FCSTD DOCUMENT  (FreeCAD 1.0R39109 (Git))
Label: udemyProjectModule1metricFREECAD
License: All rights reserved
objects: Part::FeaturePython×3, Sketcher::SketchObject×1
note: 5 computed .brp shape members not serialized (recipe doc carries the construction recipe); baked Part::Feature solids carry a one-line shape summary decoded from their .brp

FEATURE [Part::FeaturePython] IfcObject003  label="Building"  # WARN: FeaturePython — macro-defined, semantics opaque (R4)
  CompositionType = -1
  ElevationOfRefHeight = 0
  ElevationOfTerrain = 0
  GlobalId = 3ZR71QWXn8eBFc1LVgS9kI
  IfcClass = IfcBuilding
  ShapeMode = 0
  StepId = 23
  expr: Label2 = Description
FEATURE [Part::FeaturePython] IfcObject002  label="Site"  # WARN: FeaturePython — macro-defined, semantics opaque (R4)
  CompositionType = -1
  GlobalId = 3sOkh7jo544A_tfJeOJWge
  Group = -> [IfcObject003]
  IfcClass = IfcSite
  RefElevation = 0
  ShapeMode = 0
  StepId = 21
  expr: Label2 = Description
FEATURE [Part::FeaturePython] IfcObject001  label="_IfcProject001"  # WARN: FeaturePython — macro-defined, semantics opaque (R4)
  GlobalId = 2x7dZLKtn7CQsyYiZBJNY$
  Group = -> [IfcObject002]
  IfcClass = IfcProject
  IfcFilePath = <userpath>/github/websiteRepository/udemyCADcert/udemyProjectModule1metricFREECAD.ifc
  Modified = true
  Schema = 1
  ShapeMode = 0
  StepId = 1
  expr: Label2 = Description
FEATURE [Sketcher::SketchObject] Sketch  label="floorplan"
  ArcFitTolerance = 1e-06
  FullyConstrained = false
  MakeInternals = false
  sketch-geometry (38):
    g0: LineSegment StartX=0 StartY=0 StartZ=0 EndX=20000 EndY=0 EndZ=0
    g1: LineSegment StartX=20000 StartY=0 StartZ=0 EndX=20000 EndY=10000 EndZ=0
    g2: LineSegment StartX=20000 StartY=10000 StartZ=0 EndX=0 EndY=10000 EndZ=0
    g3: LineSegment StartX=0 StartY=10000 StartZ=0 EndX=0 EndY=0 EndZ=0
    g4: LineSegment [constr] StartX=0 StartY=5000 StartZ=0 EndX=300 EndY=5000 EndZ=0
    g5: LineSegment [constr] StartX=10000 StartY=10000 StartZ=0 EndX=10000 EndY=9700 EndZ=0
    g6: LineSegment [constr] StartX=10000 StartY=0 StartZ=0 EndX=10000 EndY=300 EndZ=0
    g7: LineSegment [constr] StartX=20000 StartY=5000 StartZ=0 EndX=19700 EndY=5000 EndZ=0
    g8: LineSegment StartX=300 StartY=300 StartZ=0 EndX=19700 EndY=300 EndZ=0
    g9: LineSegment StartX=19700 StartY=300 StartZ=0 EndX=19700 EndY=9700 EndZ=0
    g10: LineSegment StartX=19700 StartY=9700 StartZ=0 EndX=300 EndY=9700 EndZ=0
    g11: LineSegment StartX=300 StartY=9700 StartZ=0 EndX=300 EndY=300 EndZ=0
    g12: LineSegment [constr] StartX=300 StartY=9700 StartZ=0 EndX=4500 EndY=9700 EndZ=0
    g13: LineSegment StartX=4500 StartY=9700 StartZ=0 EndX=4500 EndY=6100 EndZ=0
    g14: LineSegment [constr] StartX=4500 StartY=9700 StartZ=0 EndX=4400 EndY=9700 EndZ=0
    g15: LineSegment StartX=4400 StartY=9700 StartZ=0 EndX=4400 EndY=6100 EndZ=0
    g16: LineSegment StartX=10600 StartY=9700 StartZ=0 EndX=10600 EndY=6100 EndZ=0
    g17: LineSegment StartX=10500 StartY=9700 StartZ=0 EndX=10500 EndY=6100 EndZ=0
    g18: LineSegment StartX=16600 StartY=9700 StartZ=0 EndX=16600 EndY=6100 EndZ=0
    g19: LineSegment StartX=16700 StartY=9700 StartZ=0 EndX=16700 EndY=6100 EndZ=0
    g20: LineSegment StartX=16700 StartY=9700 StartZ=0 EndX=16700 EndY=6100 EndZ=0
    g21: LineSegment StartX=300 StartY=3900 StartZ=0 EndX=4400 EndY=3900 EndZ=0
    g22: LineSegment StartX=300 StartY=4000 StartZ=0 EndX=16700 EndY=4000 EndZ=0
    g23: LineSegment StartX=300 StartY=6100 StartZ=0 EndX=4400 EndY=6100 EndZ=0
    g24: LineSegment StartX=19700 StartY=6000 StartZ=0 EndX=300 EndY=6000 EndZ=0
    g25: LineSegment StartX=4500 StartY=3900 StartZ=0 EndX=4500 EndY=300 EndZ=0
    g26: LineSegment StartX=4500 StartY=6100 StartZ=0 EndX=10500 EndY=6100 EndZ=0
    g27: LineSegment StartX=4400 StartY=3900 StartZ=0 EndX=4400 EndY=300 EndZ=0
    g28: LineSegment StartX=4500 StartY=3900 StartZ=0 EndX=10500 EndY=3900 EndZ=0
    g29: LineSegment StartX=10600 StartY=6100 StartZ=0 EndX=16600 EndY=6100 EndZ=0
    g30: LineSegment StartX=10500 StartY=3900 StartZ=0 EndX=10500 EndY=300 EndZ=0
    g31: LineSegment StartX=10600 StartY=3900 StartZ=0 EndX=10600 EndY=300 EndZ=0
    g32: LineSegment StartX=10600 StartY=3900 StartZ=0 EndX=16600 EndY=3900 EndZ=0
    g33: LineSegment StartX=16600 StartY=3900 StartZ=0 EndX=16600 EndY=300 EndZ=0
    g34: LineSegment StartX=16700 StartY=4000 StartZ=0 EndX=16700 EndY=300 EndZ=0
    g35: LineSegment StartX=16700 StartY=6100 StartZ=0 EndX=19700 EndY=6100 EndZ=0
    g36: LineSegment StartX=16700 StartY=4000 StartZ=0 EndX=16700 EndY=300 EndZ=0
    g37: GeomPoint X=30000 Y=12000 Z=0
  constraints (115):
    c: Coincident(g0,g1)
    c: Coincident(g1,g2)
    c: Coincident(g2,g3)
    c: Coincident(g3,g0)
    c: Horizontal(g0)
    c: Horizontal(g2)
    c: Vertical(g1)
    c: Vertical(g3)
    c: Distance(g1,g3) = 20000
    c: Distance(g0,g2) = 10000
    c: Coincident(g0,g-1)
    c: Distance(g4) = 300
    c: Horizontal(g4)
    c: Symmetric(g3,g3,g4)
    c: Distance(g5) = 300
    c: Symmetric(g2,g2,g5)
    c: Vertical(g5)
    c: Distance(g6) = 300
    c: Symmetric(g0,g0,g6)
    c: Vertical(g6)
    c: Distance(g7) = 300
    c: Symmetric(g1,g1,g7)
    c: Horizontal(g7)
    c: Coincident(g8,g9)
    c: Coincident(g9,g10)
    c: Coincident(g10,g11)
    c: Coincident(g11,g8)
    c: Horizontal(g8)
    c: Horizontal(g10)
    c: Vertical(g9)
    c: Vertical(g11)
    c: PointOnObject(g6,g8)
    c: PointOnObject(g4,g11)
    c: PointOnObject(g5,g10)
    c: PointOnObject(g7,g9)
    c: Horizontal(g12)
    c: Coincident(g12,g10)
    c: Coincident(g13,g12)
    c: Vertical(g13)
    c: Distance(g14) = 100
    c: Horizontal(g14)
    c: Coincident(g14,g12)
    c: Coincident(g15,g14)
    c: PointOnObject(g27,g8)
    c: PointOnObject(g25,g8)
    c: Vertical(g15)
    c: PointOnObject(g16,g10)
    c: PointOnObject(g31,g8)
    c: Vertical(g16)
    c: PointOnObject(g17,g10)
    c: PointOnObject(g30,g8)
    c: Vertical(g17)
    c: Distance(g16,g17) = 100
    c: PointOnObject(g18,g10)
    c: PointOnObject(g33,g8)
    c: Vertical(g18)
    c: Distance(g16,g18) = 6000
    c: Distance(g13,g17) = 6000
    c: Distance(g11,g15) = 4100
    c: PointOnObject(g19,g10)
    c: PointOnObject(g34,g8)
    c: Vertical(g19)
    c: Distance(g19,g18) = 100
    c: PointOnObject(g20,g10)
    c: PointOnObject(g36,g8)
    c: Vertical(g20)
    c: Distance(g9,g20) = 3000
    c: PointOnObject(g21,g11)
    c: Horizontal(g21)
    c: Distance(g8,g21) = 3600
    c: PointOnObject(g22,g11)
    c: Horizontal(g22)
    c: Distance(g22,g21) = 100
    c: PointOnObject(g23,g11)
    c: PointOnObject(g35,g9)
    c: Horizontal(g23)
    c: Distance(g10,g23) = 3600
    c: PointOnObject(g24,g9)
    c: PointOnObject(g24,g11)
    c: Horizontal(g24)
    c: Distance(g23,g24) = 100
    c: PointOnObject(g13,g26)
    c: PointOnObject(g26,g13)
    c: Coincident(g15,g23)
    c: Coincident(g27,g21)
    c: Coincident(g25,g28)
    c: Coincident(g17,g26)
    c: Coincident(g16,g29)
    c: Coincident(g31,g32)
    c: Coincident(g30,g28)
    c: Coincident(g19,g35)
    c: Coincident(g18,g29)
    c: PointOnObject(g36,g22)
    c: Coincident(g33,g32)
    c: Coincident(g22,g34)
    c: Distance(g37,g-2) = 30000
    c: Distance(g37,g-1) = 12000
    c: DistanceX(g31,g32) = 6000
    c: DistanceX(g25,g28) = 6000
    c: Distance(g28,g31) = 100
    c: Distance(g21,g25) = 100
    c: Distance(g13,g24) = 100
    c: Distance(g17,g24) = 100
    c: Distance(g16,g24) = 100
    c: Distance(g20,g24) = 100
    c: Distance(g34,g33) = 100
    c: Distance(g32,g34) = 100
    c: Distance(g31,g22) = 100
    c: Perpendicular(g8,g27)
    c: Perpendicular(g8,g25)
    c: Perpendicular(g18,g29)
    c: Parallel(g32,g8)
    c: Parallel(g34,g9)
    c: Parallel(g30,g11)
    c: Parallel(g35,g24)
